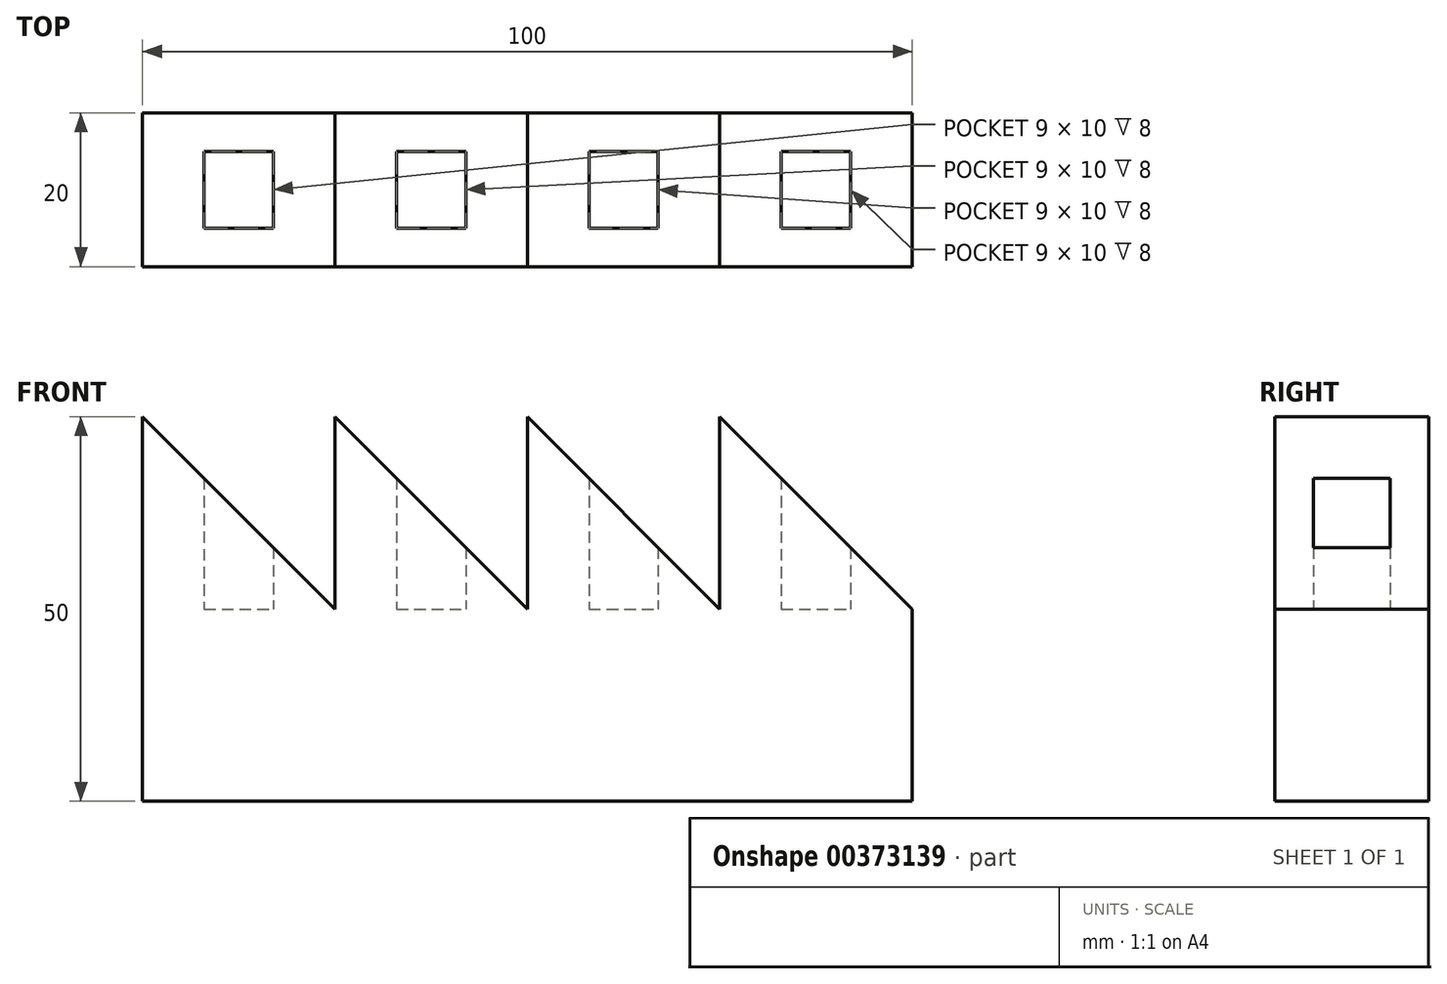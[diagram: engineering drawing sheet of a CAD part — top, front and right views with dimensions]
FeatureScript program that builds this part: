
annotation { "Feature Type Name" : "Feature", "Feature Type Description" : "" }
export const myFeature = defineFeature(function(context is Context, id is Id, definition is map)
    precondition{}
    {
        {
            var Q0;
            Q0=qCreatedBy(makeId("Front.planeOp"),FACE);
            var sketch = newSketch(context, id + "F0", { "sketchPlane" : qUnion([Q0])});
            skLineSegment(sketch, "E0", {"start": v(-58.47, 0) * mm, "end": v(-58.47, 25) * mm});
            skLineSegment(sketch, "E1", {"start": v(-58.47, 25) * mm, "end": v(-33.47, 0) * mm});
            skLineSegment(sketch, "E2", {"start": v(-58.47, 0) * mm, "end": v(-58.47, -25) * mm});
            skLineSegment(sketch, "E3", {"start": v(-58.47, -25) * mm, "end": v(41.53, -25) * mm});
            skLineSegment(sketch, "E4", {"start": v(41.53, -25) * mm, "end": v(41.53, 0) * mm});
            skLineSegment(sketch, "E5", {"start": v(-50.47, 17) * mm, "end": v(-50.47, 0) * mm});
            skLineSegment(sketch, "E6", {"start": v(-41.47, 8) * mm, "end": v(-41.47, 0) * mm});
            skLineSegment(sketch, "E7", {"start": v(-33.47, 0) * mm, "end": v(-33.47, 25) * mm});
            skLineSegment(sketch, "E8", {"start": v(-33.47, 25) * mm, "end": v(-8.47, 0) * mm});
            skLineSegment(sketch, "E9", {"start": v(-25.47, 17) * mm, "end": v(-25.47, 0) * mm});
            skLineSegment(sketch, "E10", {"start": v(-16.47, 8) * mm, "end": v(-16.47, 0) * mm});
            skLineSegment(sketch, "E11", {"start": v(-8.47, 0) * mm, "end": v(-8.47, 25) * mm});
            skLineSegment(sketch, "E12", {"start": v(-8.47, 25) * mm, "end": v(16.53, 0) * mm});
            skLineSegment(sketch, "E13", {"start": v(-0.47, 17) * mm, "end": v(-0.47, 0) * mm});
            skLineSegment(sketch, "E14", {"start": v(8.53, 8) * mm, "end": v(8.53, 0) * mm});
            skLineSegment(sketch, "E15", {"start": v(16.53, 0) * mm, "end": v(16.53, 25) * mm});
            skLineSegment(sketch, "E16", {"start": v(16.53, 25) * mm, "end": v(41.53, 0) * mm});
            skLineSegment(sketch, "E17", {"start": v(24.53, 17) * mm, "end": v(24.53, 0) * mm});
            skLineSegment(sketch, "E18", {"start": v(33.53, 8) * mm, "end": v(33.53, 0) * mm});
            skLineSegment(sketch, "E19", {"start": v(-50.47, 0) * mm, "end": v(-41.47, 0) * mm});
            skLineSegment(sketch, "E20", {"start": v(-25.47, 0) * mm, "end": v(-16.47, 0) * mm});
            skLineSegment(sketch, "E21", {"start": v(-0.47, 0) * mm, "end": v(8.53, 0) * mm});
            skLineSegment(sketch, "E22", {"start": v(24.53, 0) * mm, "end": v(33.53, 0) * mm});
            skSolve(sketch);
        }
        {
            var Q0;
            {var subQ15=sQuery(id+"F0.wireOp",EDGE,"E0");Q0=makeQuery(id+"F0.imprint","IMPRINT",FACE,{"disambiguationData":[TD([[makeQuery(id+"F0.imprint","IMPRINT",EDGE,{"derivedFrom":subQ15}),-1.0]])]});}
            var Q1;
            {var subQ0=sQuery(id+"F0.wireOp",EDGE,"E17");Q1=makeQuery(id+"F0.imprint","IMPRINT",FACE,{"disambiguationData":[TD([[makeQuery(id+"F0.imprint","IMPRINT",EDGE,{"derivedFrom":subQ0}),1.0]])]});}
            var Q2;
            {var subQ0=sQuery(id+"F0.wireOp",EDGE,"E13");Q2=makeQuery(id+"F0.imprint","IMPRINT",FACE,{"disambiguationData":[TD([[makeQuery(id+"F0.imprint","IMPRINT",EDGE,{"derivedFrom":subQ0}),1.0]])]});}
            var Q3;
            {var subQ0=sQuery(id+"F0.wireOp",EDGE,"E9");Q3=makeQuery(id+"F0.imprint","IMPRINT",FACE,{"disambiguationData":[TD([[makeQuery(id+"F0.imprint","IMPRINT",EDGE,{"derivedFrom":subQ0}),1.0]])]});}
            var Q4;
            {var subQ0=sQuery(id+"F0.wireOp",EDGE,"E5");Q4=makeQuery(id+"F0.imprint","IMPRINT",FACE,{"disambiguationData":[TD([[makeQuery(id+"F0.imprint","IMPRINT",EDGE,{"derivedFrom":subQ0}),1.0]])]});}
            extrude(context, id + "F1", {"entities" : qUnion([Q0, Q1, Q2, Q3, Q4]), "depth" : 20 * mm});
        }
        {
            var Q0;
            Q0=makeQuery(id+"F1.opExtrude","SWEPT_BODY",BODY,{"disambiguationData":[OSD([sQuery(id+"F0.wireOp",EDGE,"E0"),sQuery(id+"F0.wireOp",EDGE,"E1"),sQuery(id+"F0.wireOp",EDGE,"E2"),sQuery(id+"F0.wireOp",EDGE,"E3"),sQuery(id+"F0.wireOp",EDGE,"E4"),sQuery(id+"F0.wireOp",EDGE,"E7"),sQuery(id+"F0.wireOp",EDGE,"E8"),sQuery(id+"F0.wireOp",EDGE,"E11"),sQuery(id+"F0.wireOp",EDGE,"E12"),sQuery(id+"F0.wireOp",EDGE,"E15"),sQuery(id+"F0.wireOp",EDGE,"E16")])]});
            transform(context, id + "F2", {"entities" : qUnion([Q0]), "transformType" : TransformType.TRANSLATION_3D, "dx" : 0 * mm, "dy" : 10 * mm, "dz" : 0 * mm, "makeCopy" : false});
        }
        {
            var Q0;
            {var subQ0=sQuery(id+"F0.wireOp",EDGE,"E17");Q0=makeQuery(id+"F0.imprint","IMPRINT",FACE,{"disambiguationData":[TD([[makeQuery(id+"F0.imprint","IMPRINT",EDGE,{"derivedFrom":subQ0}),1.0]])]});}
            var Q1;
            {var subQ0=sQuery(id+"F0.wireOp",EDGE,"E13");Q1=makeQuery(id+"F0.imprint","IMPRINT",FACE,{"disambiguationData":[TD([[makeQuery(id+"F0.imprint","IMPRINT",EDGE,{"derivedFrom":subQ0}),1.0]])]});}
            var Q2;
            {var subQ0=sQuery(id+"F0.wireOp",EDGE,"E9");Q2=makeQuery(id+"F0.imprint","IMPRINT",FACE,{"disambiguationData":[TD([[makeQuery(id+"F0.imprint","IMPRINT",EDGE,{"derivedFrom":subQ0}),1.0]])]});}
            var Q3;
            {var subQ0=sQuery(id+"F0.wireOp",EDGE,"E5");Q3=makeQuery(id+"F0.imprint","IMPRINT",FACE,{"disambiguationData":[TD([[makeQuery(id+"F0.imprint","IMPRINT",EDGE,{"derivedFrom":subQ0}),1.0]])]});}
            extrude(context, id + "F3", {"entities" : qUnion([Q0, Q1, Q2, Q3]), "operationType" : NewBodyOperationType.REMOVE, "depth" : 5 * mm, "hasSecondDirection" : true, "secondDirectionOppositeDirection" : true, "secondDirectionDepth" : 5 * mm});
        }
    });
